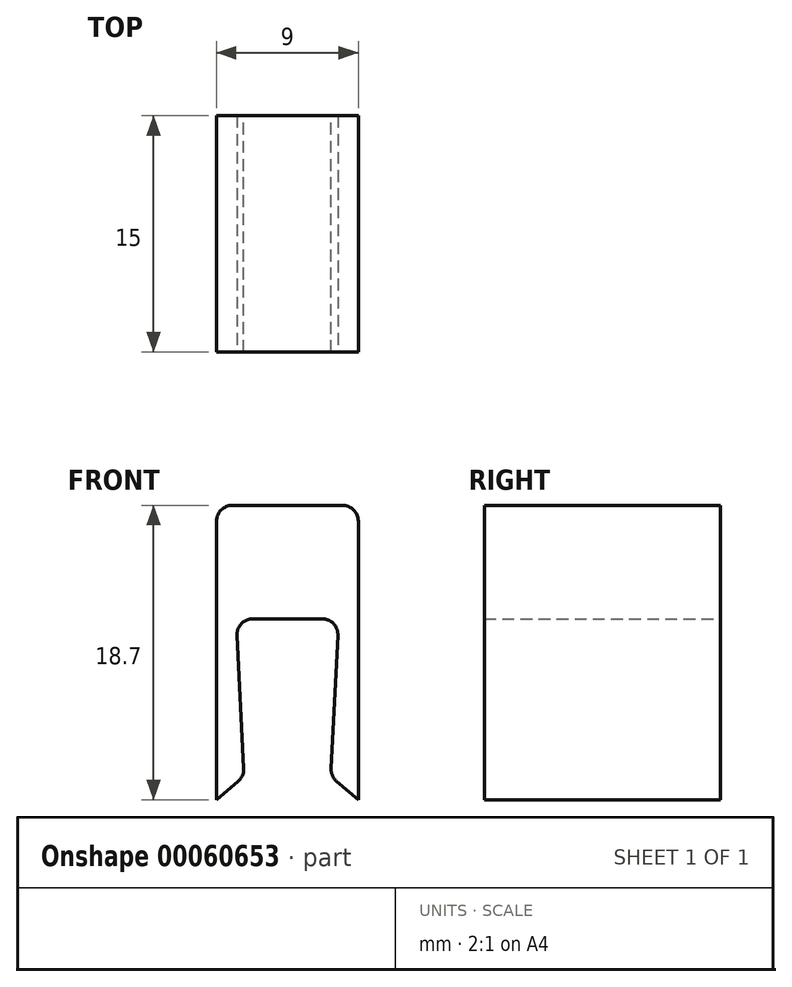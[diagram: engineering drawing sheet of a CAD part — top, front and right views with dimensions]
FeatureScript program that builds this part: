
annotation { "Feature Type Name" : "Feature", "Feature Type Description" : "" }
export const myFeature = defineFeature(function(context is Context, id is Id, definition is map)
    precondition{}
    {
        {
            var Q0;
            Q0=qCreatedBy(makeId("Front.planeOp"),FACE);
            var sketch = newSketch(context, id + "F0", { "sketchPlane" : qUnion([Q0])});
            skLineSegment(sketch, "E0", {"start": v(-4.5, -18.7) * mm, "end": v(-2.75, -17.2) * mm});
            skLineSegment(sketch, "E1", {"start": v(-2.75, -17.2) * mm, "end": v(-3.25, -7.2) * mm});
            skLineSegment(sketch, "E2", {"start": v(-3.25, -7.2) * mm, "end": v(3.25, -7.2) * mm});
            skLineSegment(sketch, "E3", {"start": v(3.25, -7.2) * mm, "end": v(2.75, -17.2) * mm});
            skLineSegment(sketch, "E4", {"start": v(2.75, -17.2) * mm, "end": v(4.5, -18.7) * mm});
            skLineSegment(sketch, "E5", {"start": v(4.5, -1) * mm, "end": v(4.5, -18.7) * mm});
            skLineSegment(sketch, "E6", {"start": v(4.5, -1) * mm, "end": v(4.5, 0) * mm});
            skLineSegment(sketch, "E7", {"start": v(4.5, 0) * mm, "end": v(-4.5, 0) * mm});
            skLineSegment(sketch, "E8", {"start": v(-4.5, 0) * mm, "end": v(-4.5, -18.7) * mm});
            skLineSegment(sketch, "E9", {"start": v(-2.75, -17.2) * mm, "end": v(2.75, -17.2) * mm, "construction": true});
            skPoint(sketch, "E10", {"position": v(0, 0) * mm});
            skPoint(sketch, "E11", {"position": v(0, -7.2) * mm});
            skPoint(sketch, "E12", {"position": v(0, -17.2) * mm});
            skLineSegment(sketch, "E13", {"start": v(-4.5, -18.7) * mm, "end": v(4.5, -18.7) * mm, "construction": true});
            skSolve(sketch);
        }
        {
            var Q0;
            Q0=makeQuery(id+"F0.imprint","IMPRINT",FACE,{"disambiguationData":[TD([[makeQuery(id+"F0.imprint","IMPRINT",EDGE,{"derivedFrom":sQuery(id+"F0.wireOp",EDGE,"E0")}),1.0]])]});
            extrude(context, id + "F1", {"entities" : qUnion([Q0]), "offsetDistance" : 25 * mm, "depth" : 15 * mm});
        }
        {
            var Q0;
            Q0=makeQuery(id+"F1.opExtrude","SWEPT_EDGE",EDGE,{"disambiguationData":[OSD([sQuery(id+"F0.wireOp",EDGE,"E0"),sQuery(id+"F0.wireOp",EDGE,"E1")])]});
            var Q1;
            Q1=makeQuery(id+"F1.opExtrude","SWEPT_EDGE",EDGE,{"disambiguationData":[OSD([sQuery(id+"F0.wireOp",EDGE,"E7"),sQuery(id+"F0.wireOp",EDGE,"E8")])]});
            var Q2;
            Q2=makeQuery(id+"F1.opExtrude","SWEPT_EDGE",EDGE,{"disambiguationData":[OSD([sQuery(id+"F0.wireOp",EDGE,"E6"),sQuery(id+"F0.wireOp",EDGE,"E7")])]});
            var Q3;
            Q3=makeQuery(id+"F1.opExtrude","SWEPT_EDGE",EDGE,{"disambiguationData":[OSD([sQuery(id+"F0.wireOp",EDGE,"E3"),sQuery(id+"F0.wireOp",EDGE,"E4")])]});
            fillet(context, id + "F2", {"entities" : qUnion([Q0, Q1, Q2, Q3]), "radius" : 1 * mm, "tangentPropagation" : true, "allowEdgeOverflow" : false});
        }
        {
            var Q0;
            Q0=makeQuery(id+"F1.opExtrude","SWEPT_EDGE",EDGE,{"disambiguationData":[OSD([sQuery(id+"F0.wireOp",EDGE,"E1"),sQuery(id+"F0.wireOp",EDGE,"E2")])]});
            var Q1;
            Q1=makeQuery(id+"F1.opExtrude","SWEPT_EDGE",EDGE,{"disambiguationData":[OSD([sQuery(id+"F0.wireOp",EDGE,"E2"),sQuery(id+"F0.wireOp",EDGE,"E3")])]});
            fillet(context, id + "F3", {"entities" : qUnion([Q0, Q1]), "radius" : 1 * mm, "tangentPropagation" : true, "allowEdgeOverflow" : false});
        }
    });
